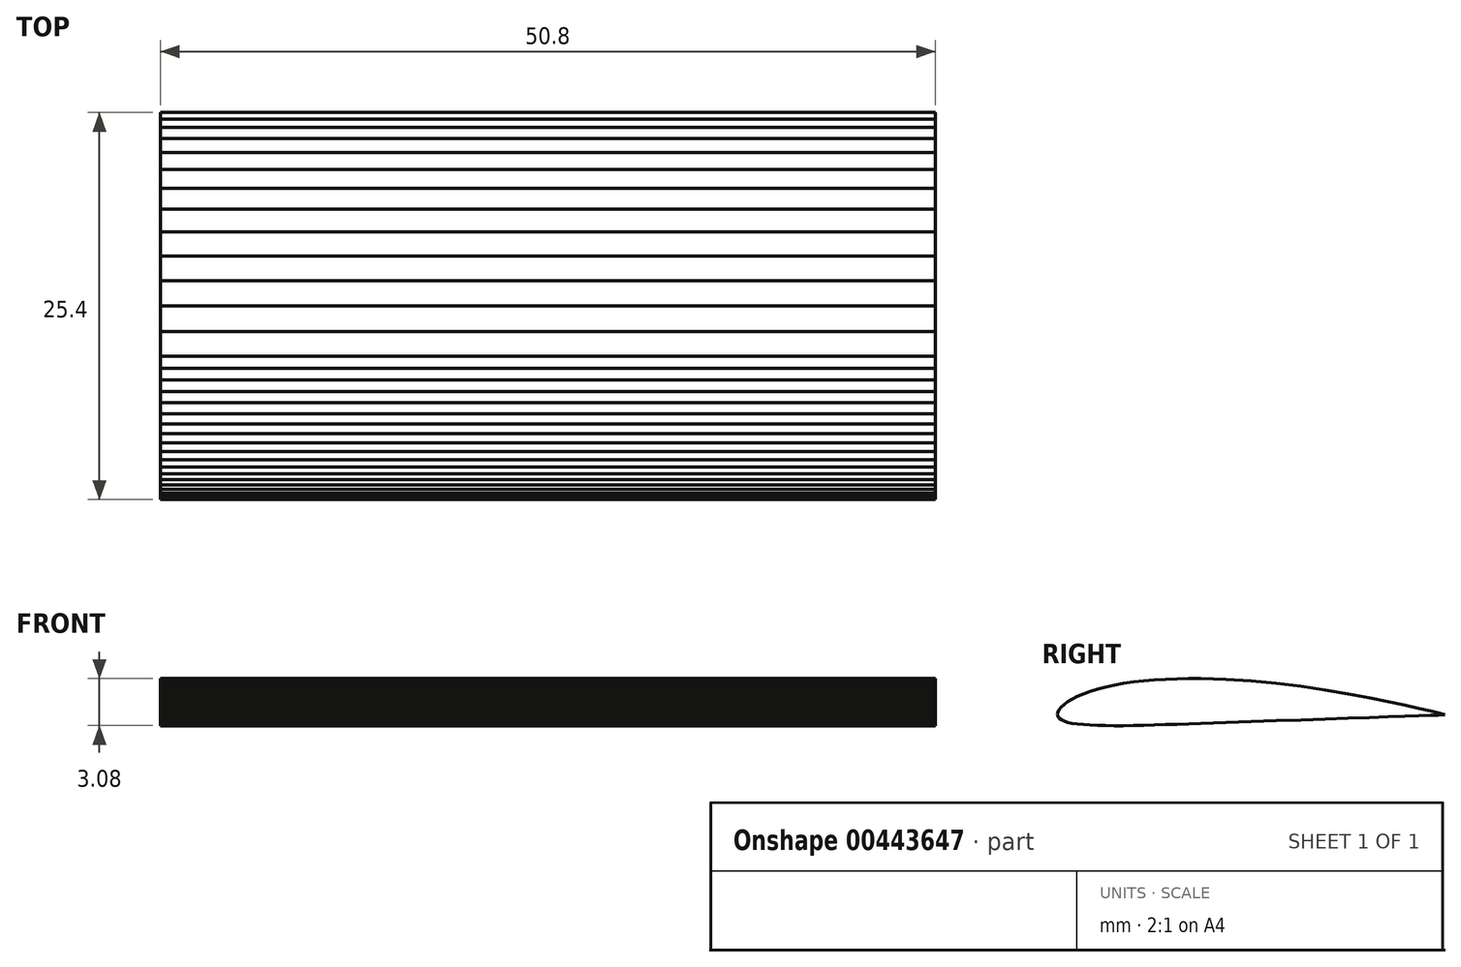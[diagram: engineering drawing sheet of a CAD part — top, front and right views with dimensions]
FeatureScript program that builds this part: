
annotation { "Feature Type Name" : "Feature", "Feature Type Description" : "" }
export const myFeature = defineFeature(function(context is Context, id is Id, definition is map)
    precondition{}
    {
        {
            var Q0;
            Q0=qCreatedBy(makeId("Right.planeOp"),FACE);
            var sketch = newSketch(context, id + "F0", { "sketchPlane" : qUnion([Q0])});
            skLineSegment(sketch, "E0", {"start": v(12.7, -0.82) * mm, "end": v(12.6, -0.8) * mm});
            skLineSegment(sketch, "E1", {"start": v(12.6, -0.8) * mm, "end": v(12.27, -0.7) * mm});
            skLineSegment(sketch, "E2", {"start": v(12.27, -0.7) * mm, "end": v(11.73, -0.58) * mm});
            skLineSegment(sketch, "E3", {"start": v(11.73, -0.58) * mm, "end": v(11, -0.4) * mm});
            skLineSegment(sketch, "E4", {"start": v(11, -0.4) * mm, "end": v(10.08, -0.2) * mm});
            skLineSegment(sketch, "E5", {"start": v(10.08, -0.2) * mm, "end": v(8.98, 0.04) * mm});
            skLineSegment(sketch, "E6", {"start": v(8.98, 0.04) * mm, "end": v(7.73, 0.3) * mm});
            skLineSegment(sketch, "E7", {"start": v(7.73, 0.3) * mm, "end": v(6.35, 0.55) * mm});
            skLineSegment(sketch, "E8", {"start": v(6.35, 0.55) * mm, "end": v(4.86, 0.8) * mm});
            skLineSegment(sketch, "E9", {"start": v(4.86, 0.8) * mm, "end": v(3.29, 1.04) * mm});
            skLineSegment(sketch, "E10", {"start": v(3.29, 1.04) * mm, "end": v(1.66, 1.24) * mm});
            skLineSegment(sketch, "E11", {"start": v(1.66, 1.24) * mm, "end": v(0, 1.4) * mm});
            skLineSegment(sketch, "E12", {"start": v(0, 1.4) * mm, "end": v(-1.66, 1.5) * mm});
            skLineSegment(sketch, "E13", {"start": v(-1.66, 1.5) * mm, "end": v(-3.29, 1.54) * mm});
            skLineSegment(sketch, "E14", {"start": v(-3.29, 1.54) * mm, "end": v(-4.08, 1.54) * mm});
            skLineSegment(sketch, "E15", {"start": v(-4.08, 1.54) * mm, "end": v(-4.86, 1.53) * mm});
            skLineSegment(sketch, "E16", {"start": v(-4.86, 1.53) * mm, "end": v(-5.62, 1.5) * mm});
            skLineSegment(sketch, "E17", {"start": v(-5.62, 1.5) * mm, "end": v(-6.35, 1.46) * mm});
            skLineSegment(sketch, "E18", {"start": v(-6.35, 1.46) * mm, "end": v(-7.06, 1.4) * mm});
            skLineSegment(sketch, "E19", {"start": v(-7.06, 1.4) * mm, "end": v(-7.73, 1.33) * mm});
            skLineSegment(sketch, "E20", {"start": v(-7.73, 1.33) * mm, "end": v(-8.37, 1.24) * mm});
            skLineSegment(sketch, "E21", {"start": v(-8.37, 1.24) * mm, "end": v(-8.98, 1.12) * mm});
            skLineSegment(sketch, "E22", {"start": v(-8.98, 1.12) * mm, "end": v(-9.55, 0.99) * mm});
            skLineSegment(sketch, "E23", {"start": v(-9.55, 0.99) * mm, "end": v(-10.08, 0.84) * mm});
            skLineSegment(sketch, "E24", {"start": v(-10.08, 0.84) * mm, "end": v(-10.56, 0.69) * mm});
            skLineSegment(sketch, "E25", {"start": v(-10.56, 0.69) * mm, "end": v(-11, 0.53) * mm});
            skLineSegment(sketch, "E26", {"start": v(-11, 0.53) * mm, "end": v(-11.4, 0.37) * mm});
            skLineSegment(sketch, "E27", {"start": v(-11.4, 0.37) * mm, "end": v(-11.73, 0.2) * mm});
            skLineSegment(sketch, "E28", {"start": v(-11.73, 0.2) * mm, "end": v(-12.03, 0.03) * mm});
            skLineSegment(sketch, "E29", {"start": v(-12.03, 0.03) * mm, "end": v(-12.27, -0.15) * mm});
            skLineSegment(sketch, "E30", {"start": v(-12.27, -0.15) * mm, "end": v(-12.46, -0.33) * mm});
            skLineSegment(sketch, "E31", {"start": v(-12.46, -0.33) * mm, "end": v(-12.6, -0.5) * mm});
            skLineSegment(sketch, "E32", {"start": v(-12.6, -0.5) * mm, "end": v(-12.67, -0.67) * mm});
            skLineSegment(sketch, "E33", {"start": v(-12.67, -0.67) * mm, "end": v(-12.7, -0.81) * mm});
            skLineSegment(sketch, "E34", {"start": v(-12.7, -0.81) * mm, "end": v(-12.67, -0.94) * mm});
            skLineSegment(sketch, "E35", {"start": v(-12.67, -0.94) * mm, "end": v(-12.6, -1.05) * mm});
            skLineSegment(sketch, "E36", {"start": v(-12.6, -1.05) * mm, "end": v(-12.46, -1.15) * mm});
            skLineSegment(sketch, "E37", {"start": v(-12.46, -1.15) * mm, "end": v(-12.27, -1.24) * mm});
            skLineSegment(sketch, "E38", {"start": v(-12.27, -1.24) * mm, "end": v(-12.03, -1.32) * mm});
            skLineSegment(sketch, "E39", {"start": v(-12.03, -1.32) * mm, "end": v(-11.73, -1.39) * mm});
            skLineSegment(sketch, "E40", {"start": v(-11.73, -1.39) * mm, "end": v(-11.4, -1.44) * mm});
            skLineSegment(sketch, "E41", {"start": v(-11.4, -1.44) * mm, "end": v(-11, -1.47) * mm});
            skLineSegment(sketch, "E42", {"start": v(-11, -1.47) * mm, "end": v(-10.56, -1.5) * mm});
            skLineSegment(sketch, "E43", {"start": v(-10.56, -1.5) * mm, "end": v(-10.08, -1.52) * mm});
            skLineSegment(sketch, "E44", {"start": v(-10.08, -1.52) * mm, "end": v(-9.55, -1.54) * mm});
            skLineSegment(sketch, "E45", {"start": v(-9.55, -1.54) * mm, "end": v(-8.98, -1.54) * mm});
            skLineSegment(sketch, "E46", {"start": v(-8.98, -1.54) * mm, "end": v(-8.37, -1.54) * mm});
            skLineSegment(sketch, "E47", {"start": v(-8.37, -1.54) * mm, "end": v(-7.73, -1.53) * mm});
            skLineSegment(sketch, "E48", {"start": v(-7.73, -1.53) * mm, "end": v(-7.06, -1.52) * mm});
            skLineSegment(sketch, "E49", {"start": v(-7.06, -1.52) * mm, "end": v(-6.35, -1.5) * mm});
            skLineSegment(sketch, "E50", {"start": v(-6.35, -1.5) * mm, "end": v(-5.62, -1.47) * mm});
            skLineSegment(sketch, "E51", {"start": v(-5.62, -1.47) * mm, "end": v(-4.86, -1.45) * mm});
            skLineSegment(sketch, "E52", {"start": v(-4.86, -1.45) * mm, "end": v(-4.08, -1.42) * mm});
            skLineSegment(sketch, "E53", {"start": v(-4.08, -1.42) * mm, "end": v(-3.29, -1.4) * mm});
            skLineSegment(sketch, "E54", {"start": v(-3.29, -1.4) * mm, "end": v(-1.66, -1.34) * mm});
            skLineSegment(sketch, "E55", {"start": v(-1.66, -1.34) * mm, "end": v(0, -1.28) * mm});
            skLineSegment(sketch, "E56", {"start": v(0, -1.28) * mm, "end": v(1.66, -1.22) * mm});
            skLineSegment(sketch, "E57", {"start": v(1.66, -1.22) * mm, "end": v(3.29, -1.16) * mm});
            skLineSegment(sketch, "E58", {"start": v(3.29, -1.16) * mm, "end": v(4.86, -1.11) * mm});
            skLineSegment(sketch, "E59", {"start": v(4.86, -1.11) * mm, "end": v(6.35, -1.06) * mm});
            skLineSegment(sketch, "E60", {"start": v(6.35, -1.06) * mm, "end": v(7.73, -1.01) * mm});
            skLineSegment(sketch, "E61", {"start": v(7.73, -1.01) * mm, "end": v(8.98, -0.97) * mm});
            skLineSegment(sketch, "E62", {"start": v(8.98, -0.97) * mm, "end": v(10.08, -0.93) * mm});
            skLineSegment(sketch, "E63", {"start": v(10.08, -0.93) * mm, "end": v(11, -0.9) * mm});
            skLineSegment(sketch, "E64", {"start": v(11, -0.9) * mm, "end": v(11.73, -0.87) * mm});
            skLineSegment(sketch, "E65", {"start": v(11.73, -0.87) * mm, "end": v(12.27, -0.85) * mm});
            skLineSegment(sketch, "E66", {"start": v(12.27, -0.85) * mm, "end": v(12.6, -0.83) * mm});
            skLineSegment(sketch, "E67", {"start": v(12.6, -0.83) * mm, "end": v(12.7, -0.82) * mm});
            skSolve(sketch);
        }
        {
            var Q0;
            Q0=makeQuery(id+"F0.imprint","IMPRINT",FACE,{"disambiguationData":[TD([[makeQuery(id+"F0.imprint","IMPRINT",EDGE,{"derivedFrom":sQuery(id+"F0.wireOp",EDGE,"E0")}),1.0]])]});
            var Q1;
            Q1=sQuery(id+"F0.wireOp",EDGE,"E58");
            var Q2;
            Q2=sQuery(id+"F0.wireOp",EDGE,"E59");
            var Q3;
            Q3=sQuery(id+"F0.wireOp",EDGE,"E61");
            var Q4;
            Q4=sQuery(id+"F0.wireOp",EDGE,"E60");
            var Q5;
            Q5=sQuery(id+"F0.wireOp",EDGE,"E62");
            var Q6;
            Q6=sQuery(id+"F0.wireOp",EDGE,"E63");
            var Q7;
            Q7=sQuery(id+"F0.wireOp",EDGE,"E54");
            var Q8;
            Q8=sQuery(id+"F0.wireOp",EDGE,"E13");
            var Q9;
            Q9=sQuery(id+"F0.wireOp",EDGE,"E14");
            var Q10;
            Q10=sQuery(id+"F0.wireOp",EDGE,"E4");
            var Q11;
            Q11=sQuery(id+"F0.wireOp",EDGE,"E5");
            var Q12;
            Q12=sQuery(id+"F0.wireOp",EDGE,"E6");
            var Q13;
            Q13=sQuery(id+"F0.wireOp",EDGE,"E7");
            var Q14;
            Q14=sQuery(id+"F0.wireOp",EDGE,"E8");
            var Q15;
            Q15=sQuery(id+"F0.wireOp",EDGE,"E9");
            var Q16;
            Q16=sQuery(id+"F0.wireOp",EDGE,"E10");
            var Q17;
            Q17=sQuery(id+"F0.wireOp",EDGE,"E11");
            var Q18;
            Q18=sQuery(id+"F0.wireOp",EDGE,"E12");
            var Q19;
            Q19=sQuery(id+"F0.wireOp",EDGE,"E55");
            var Q20;
            Q20=sQuery(id+"F0.wireOp",EDGE,"E56");
            var Q21;
            Q21=sQuery(id+"F0.wireOp",EDGE,"E57");
            var Q22;
            Q22=sQuery(id+"F0.wireOp",EDGE,"E42");
            var Q23;
            Q23=sQuery(id+"F0.wireOp",EDGE,"E26");
            var Q24;
            Q24=sQuery(id+"F0.wireOp",EDGE,"E19");
            var Q25;
            Q25=sQuery(id+"F0.wireOp",EDGE,"E51");
            var Q26;
            Q26=sQuery(id+"F0.wireOp",EDGE,"E43");
            var Q27;
            Q27=sQuery(id+"F0.wireOp",EDGE,"E27");
            var Q28;
            Q28=sQuery(id+"F0.wireOp",EDGE,"E20");
            var Q29;
            Q29=sQuery(id+"F0.wireOp",EDGE,"E52");
            var Q30;
            Q30=sQuery(id+"F0.wireOp",EDGE,"E45");
            var Q31;
            Q31=sQuery(id+"F0.wireOp",EDGE,"E44");
            var Q32;
            Q32=sQuery(id+"F0.wireOp",EDGE,"E28");
            var Q33;
            Q33=sQuery(id+"F0.wireOp",EDGE,"E21");
            var Q34;
            Q34=sQuery(id+"F0.wireOp",EDGE,"E53");
            var Q35;
            Q35=sQuery(id+"F0.wireOp",EDGE,"E46");
            var Q36;
            Q36=sQuery(id+"F0.wireOp",EDGE,"E37");
            var Q37;
            Q37=sQuery(id+"F0.wireOp",EDGE,"E30");
            var Q38;
            Q38=sQuery(id+"F0.wireOp",EDGE,"E22");
            var Q39;
            Q39=sQuery(id+"F0.wireOp",EDGE,"E47");
            var Q40;
            Q40=sQuery(id+"F0.wireOp",EDGE,"E38");
            var Q41;
            Q41=sQuery(id+"F0.wireOp",EDGE,"E15");
            var Q42;
            Q42=sQuery(id+"F0.wireOp",EDGE,"E2");
            var Q43;
            Q43=sQuery(id+"F0.wireOp",EDGE,"E3");
            var Q44;
            Q44=sQuery(id+"F0.wireOp",EDGE,"E39");
            var Q45;
            Q45=sQuery(id+"F0.wireOp",EDGE,"E23");
            var Q46;
            Q46=sQuery(id+"F0.wireOp",EDGE,"E16");
            var Q47;
            Q47=sQuery(id+"F0.wireOp",EDGE,"E64");
            var Q48;
            Q48=sQuery(id+"F0.wireOp",EDGE,"E48");
            var Q49;
            Q49=sQuery(id+"F0.wireOp",EDGE,"E40");
            var Q50;
            Q50=sQuery(id+"F0.wireOp",EDGE,"E24");
            var Q51;
            Q51=sQuery(id+"F0.wireOp",EDGE,"E17");
            var Q52;
            Q52=sQuery(id+"F0.wireOp",EDGE,"E65");
            var Q53;
            Q53=sQuery(id+"F0.wireOp",EDGE,"E49");
            var Q54;
            Q54=sQuery(id+"F0.wireOp",EDGE,"E41");
            var Q55;
            Q55=sQuery(id+"F0.wireOp",EDGE,"E25");
            var Q56;
            Q56=sQuery(id+"F0.wireOp",EDGE,"E18");
            var Q57;
            Q57=sQuery(id+"F0.wireOp",EDGE,"E50");
            var Q58;
            Q58=sQuery(id+"F0.wireOp",EDGE,"E36");
            var Q59;
            Q59=sQuery(id+"F0.wireOp",EDGE,"E29");
            var Q60;
            Q60=sQuery(id+"F0.wireOp",EDGE,"E31");
            var Q61;
            Q61=sQuery(id+"F0.wireOp",EDGE,"E1");
            var Q62;
            Q62=sQuery(id+"F0.wireOp",EDGE,"E32");
            var Q63;
            Q63=sQuery(id+"F0.wireOp",EDGE,"E33");
            var Q64;
            Q64=sQuery(id+"F0.wireOp",EDGE,"E66");
            var Q65;
            Q65=sQuery(id+"F0.wireOp",EDGE,"E34");
            var Q66;
            Q66=sQuery(id+"F0.wireOp",EDGE,"E35");
            var Q67;
            Q67=sQuery(id+"F0.wireOp",EDGE,"E0");
            var Q68;
            Q68=sQuery(id+"F0.wireOp",EDGE,"E67");
            extrude(context, id + "F1", {"entities" : qUnion([Q0]), "bodyType" : ToolBodyType.SURFACE, "surfaceEntities" : qUnion([Q1, Q2, Q3, Q4, Q5, Q6, Q7, Q8, Q9, Q10, Q11, Q12, Q13, Q14, Q15, Q16, Q17, Q18, Q19, Q20, Q21, Q22, Q23, Q24, Q25, Q26, Q27, Q28, Q29, Q30, Q31, Q32, Q33, Q34, Q35, Q36, Q37, Q38, Q39, Q40, Q41, Q42, Q43, Q44, Q45, Q46, Q47, Q48, Q49, Q50, Q51, Q52, Q53, Q54, Q55, Q56, Q57, Q58, Q59, Q60, Q61, Q62, Q63, Q64, Q65, Q66, Q67, Q68]), "depth" : 50.8 * mm});
        }
    });
